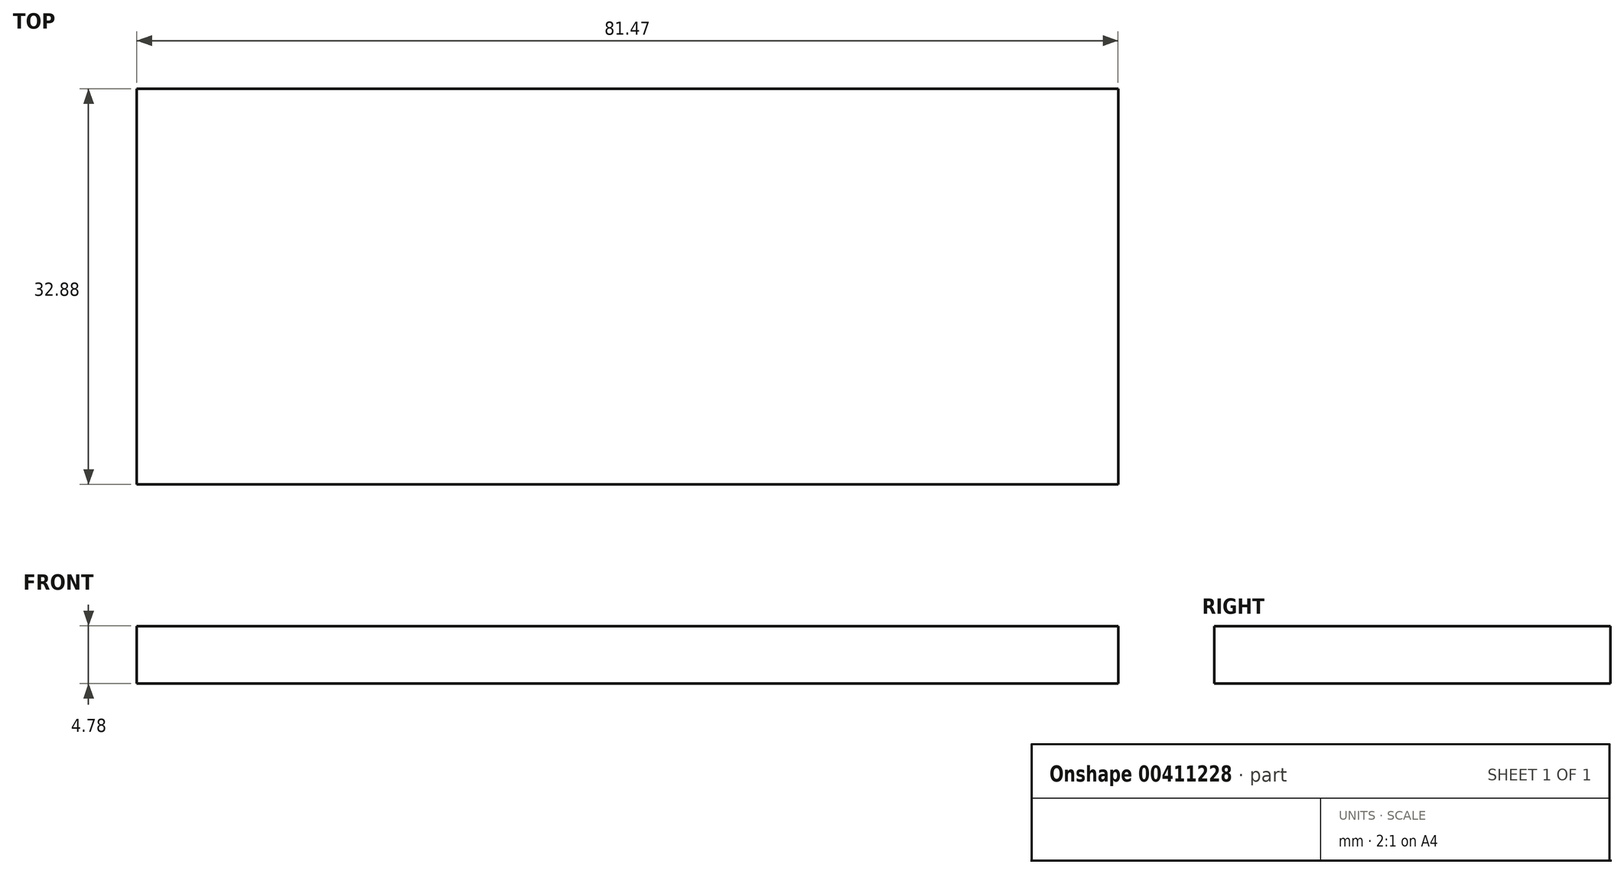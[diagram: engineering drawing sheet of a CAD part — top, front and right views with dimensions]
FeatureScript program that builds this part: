
annotation { "Feature Type Name" : "Feature", "Feature Type Description" : "" }
export const myFeature = defineFeature(function(context is Context, id is Id, definition is map)
    precondition{}
    {
        {
            var Q0;
            Q0=qCreatedBy(makeId("Top.planeOp"),FACE);
            var sketch = newSketch(context, id + "F0", { "sketchPlane" : qUnion([Q0])});
            skLineSegment(sketch, "E0.bottom", {"start": v(0, 0) * mm, "end": v(0, 0) * mm});
            skLineSegment(sketch, "E0.top", {"start": v(0, 0) * mm, "end": v(0, 0) * mm});
            skLineSegment(sketch, "E0.left", {"start": v(0, 0) * mm, "end": v(0, 0) * mm});
            skLineSegment(sketch, "E0.right", {"start": v(0, 0) * mm, "end": v(0, 0) * mm});
            skLineSegment(sketch, "E1.bottom", {"start": v(45.72, 51.3) * mm, "end": v(-35.75, 51.3) * mm});
            skLineSegment(sketch, "E1.top", {"start": v(45.72, 18.4) * mm, "end": v(-35.75, 18.4) * mm});
            skLineSegment(sketch, "E1.left", {"start": v(-35.75, 51.3) * mm, "end": v(-35.75, 18.4) * mm});
            skLineSegment(sketch, "E1.right", {"start": v(45.72, 51.3) * mm, "end": v(45.72, 18.4) * mm});
            skLineSegment(sketch, "E2.bottom", {"start": v(-35.75, 34.85) * mm, "end": v(45.72, 34.85) * mm, "construction": true});
            skLineSegment(sketch, "E2.top", {"start": v(-35.75, 34.85) * mm, "end": v(45.72, 34.85) * mm, "construction": true});
            skLineSegment(sketch, "E2.left", {"start": v(45.72, 34.85) * mm, "end": v(45.72, 34.85) * mm});
            skLineSegment(sketch, "E2.right", {"start": v(-35.75, 34.85) * mm, "end": v(-35.75, 34.85) * mm});
            skLineSegment(sketch, "E3.bottom", {"start": v(4.99, 34.85) * mm, "end": v(4.99, 34.85) * mm});
            skLineSegment(sketch, "E3.top", {"start": v(4.99, 51.3) * mm, "end": v(4.99, 51.3) * mm});
            skLineSegment(sketch, "E3.left", {"start": v(4.99, 34.85) * mm, "end": v(4.99, 51.3) * mm, "construction": true});
            skLineSegment(sketch, "E3.right", {"start": v(4.99, 34.85) * mm, "end": v(4.99, 51.3) * mm, "construction": true});
            skLineSegment(sketch, "E4.bottom", {"start": v(16.21, 18.4) * mm, "end": v(4.99, 18.4) * mm, "construction": true});
            skLineSegment(sketch, "E4.top", {"start": v(16.21, 18.4) * mm, "end": v(4.99, 18.4) * mm, "construction": true});
            skLineSegment(sketch, "E4.left", {"start": v(16.21, 18.4) * mm, "end": v(16.21, 18.4) * mm});
            skLineSegment(sketch, "E4.right", {"start": v(4.99, 18.4) * mm, "end": v(4.99, 18.4) * mm});
            skSolve(sketch);
        }
        {
            var Q0;
            Q0=makeQuery(id+"F0.imprint","IMPRINT",FACE,{"disambiguationData":[TD([[makeQuery(id+"F0.imprint","IMPRINT",EDGE,{"derivedFrom":sQuery(id+"F0.wireOp",EDGE,"E1.bottom")}),1.0]])]});
            extrude(context, id + "F1", {"entities" : qUnion([Q0]), "depth" : 4.78 * mm, "offsetDistance" : 25.4 * mm});
        }
    });
